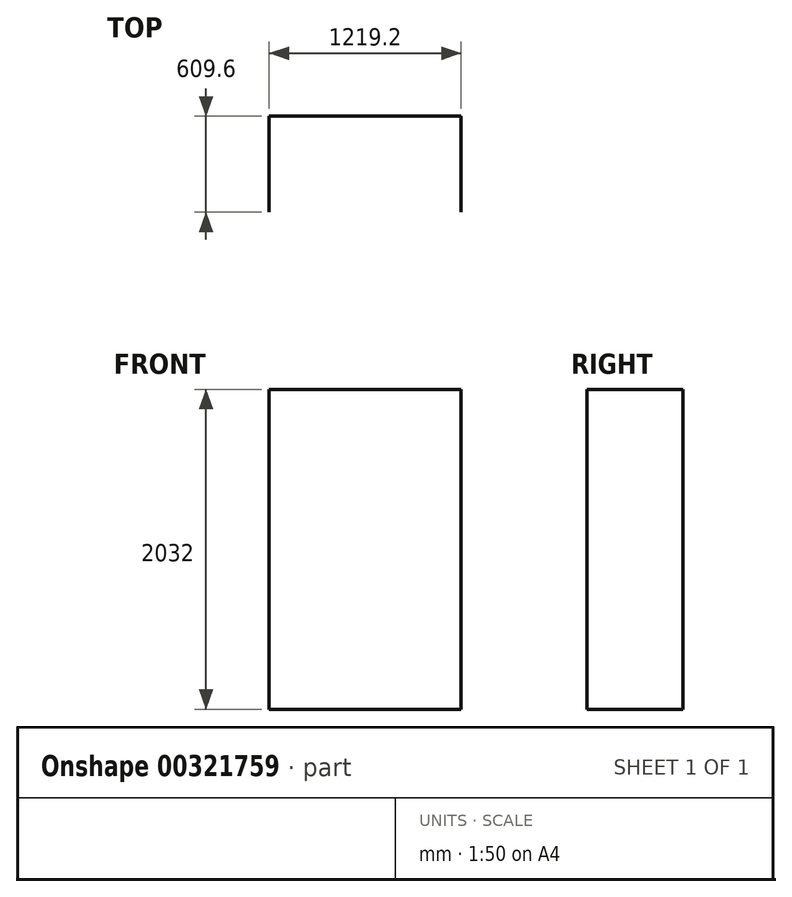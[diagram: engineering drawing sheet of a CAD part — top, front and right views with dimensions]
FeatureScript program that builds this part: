
annotation { "Feature Type Name" : "Feature", "Feature Type Description" : "" }
export const myFeature = defineFeature(function(context is Context, id is Id, definition is map)
    precondition{}
    {
        {
            var Q0;
            Q0=qCreatedBy(makeId("Top.planeOp"),FACE);
            var sketch = newSketch(context, id + "F0", { "sketchPlane" : qUnion([Q0])});
            skLineSegment(sketch, "E0.bottom", {"start": v(0, 0) * mm, "end": v(1219.2, 0) * mm});
            skLineSegment(sketch, "E0.top", {"start": v(0, 609.6) * mm, "end": v(1219.2, 609.6) * mm});
            skLineSegment(sketch, "E0.left", {"start": v(0, 0) * mm, "end": v(0, 609.6) * mm});
            skLineSegment(sketch, "E0.right", {"start": v(1219.2, 0) * mm, "end": v(1219.2, 609.6) * mm});
            skSolve(sketch);
        }
        {
            var Q0;
            Q0=sQuery(id+"F0.wireOp",EDGE,"E0.left");
            var Q1;
            Q1=sQuery(id+"F0.wireOp",EDGE,"E0.top");
            var Q2;
            Q2=sQuery(id+"F0.wireOp",EDGE,"E0.right");
            extrude(context, id + "F1", {"bodyType" : ToolBodyType.SURFACE, "surfaceEntities" : qUnion([Q0, Q1, Q2]), "depth" : 2032 * mm});
        }
    });
